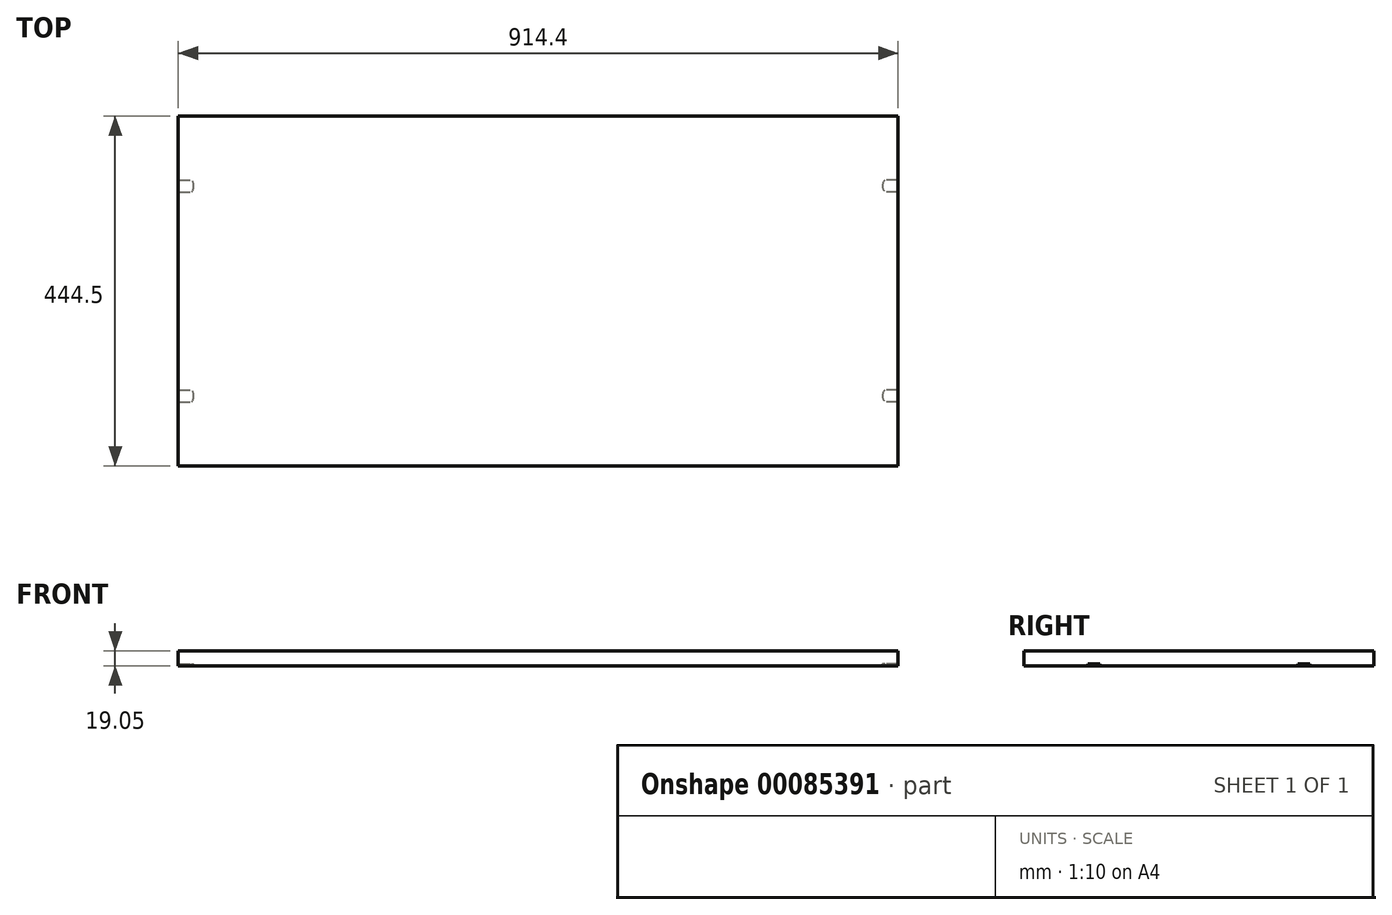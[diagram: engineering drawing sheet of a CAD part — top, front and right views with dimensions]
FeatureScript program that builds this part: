
annotation { "Feature Type Name" : "Feature", "Feature Type Description" : "" }
export const myFeature = defineFeature(function(context is Context, id is Id, definition is map)
    precondition{}
    {
        {
            var Q0;
            Q0=qCreatedBy(makeId("Top.planeOp"),FACE);
            var sketch = newSketch(context, id + "F0", { "sketchPlane" : qUnion([Q0])});
            skLineSegment(sketch, "E0.bottom", {"start": v(457.2, 222.25) * mm, "end": v(-457.2, 222.25) * mm});
            skLineSegment(sketch, "E0.top", {"start": v(457.2, -222.25) * mm, "end": v(-457.2, -222.25) * mm});
            skLineSegment(sketch, "E0.left", {"start": v(457.2, 222.25) * mm, "end": v(457.2, -222.25) * mm});
            skLineSegment(sketch, "E0.right", {"start": v(-457.2, 222.25) * mm, "end": v(-457.2, -222.25) * mm});
            skPoint(sketch, "E0.middle", {"position": v(0, 0) * mm});
            skLineSegment(sketch, "E1.bottom", {"start": v(-457.2, 126.87) * mm, "end": v(-440.94, 126.87) * mm});
            skLineSegment(sketch, "E1.top", {"start": v(-457.2, 139.83) * mm, "end": v(-440.94, 139.83) * mm});
            skLineSegment(sketch, "E1.left", {"start": v(-457.2, 126.87) * mm, "end": v(-457.2, 139.83) * mm});
            skLineSegment(sketch, "E1.right", {"start": v(-440.94, 126.87) * mm, "end": v(-440.94, 139.83) * mm});
            skArc(sketch, "E2", {"start": v(-440.94, 126.87) * mm, "mid": v(-438.66, 133.35) * mm, "end": v(-440.94, 139.83) * mm});
            skLineSegment(sketch, "E3.0", {"start": v(-457.2, 141.1) * mm, "end": v(-440.36, 141.1) * mm});
            skArc(sketch, "E4.0", {"start": v(-440.36, 125.6) * mm, "mid": v(-437.39, 133.35) * mm, "end": v(-440.36, 141.1) * mm});
            skLineSegment(sketch, "E5.0", {"start": v(-457.2, 125.6) * mm, "end": v(-440.36, 125.6) * mm});
            skLineSegment(sketch, "E6.bottom", {"start": v(-457.2, -139.83) * mm, "end": v(-440.94, -139.83) * mm});
            skLineSegment(sketch, "E6.top", {"start": v(-457.2, -126.87) * mm, "end": v(-440.94, -126.87) * mm});
            skLineSegment(sketch, "E6.left", {"start": v(-457.2, -139.83) * mm, "end": v(-457.2, -126.87) * mm});
            skLineSegment(sketch, "E6.right", {"start": v(-440.94, -139.83) * mm, "end": v(-440.94, -126.87) * mm});
            skArc(sketch, "E7", {"start": v(-440.94, -139.83) * mm, "mid": v(-438.66, -133.35) * mm, "end": v(-440.94, -126.87) * mm});
            skArc(sketch, "E8.0", {"start": v(-440.36, -141.1) * mm, "mid": v(-437.39, -133.35) * mm, "end": v(-440.36, -125.6) * mm});
            skLineSegment(sketch, "E9.0", {"start": v(-457.2, -141.1) * mm, "end": v(-440.36, -141.1) * mm});
            skLineSegment(sketch, "E10.0", {"start": v(-457.2, -125.6) * mm, "end": v(-440.36, -125.6) * mm});
            skArc(sketch, "E11.MirrorCS", {"start": v(-440.36, -125.6) * mm, "mid": v(-437.39, -133.35) * mm, "end": v(-440.36, -141.1) * mm});
            skArc(sketch, "E12.MirrorCS", {"start": v(-440.94, -126.87) * mm, "mid": v(-438.66, -133.35) * mm, "end": v(-440.94, -139.83) * mm});
            skLineSegment(sketch, "E13.MirrorCS", {"start": v(457.2, 141.1) * mm, "end": v(440.36, 141.1) * mm});
            skArc(sketch, "E14.MirrorCS", {"start": v(440.36, 125.6) * mm, "mid": v(437.39, 133.35) * mm, "end": v(440.36, 141.1) * mm});
            skLineSegment(sketch, "E15.MirrorCS", {"start": v(457.2, 125.6) * mm, "end": v(440.36, 125.6) * mm});
            skLineSegment(sketch, "E16.MirrorCS", {"start": v(457.2, -125.6) * mm, "end": v(440.36, -125.6) * mm});
            skArc(sketch, "E17.MirrorCS", {"start": v(440.36, -125.6) * mm, "mid": v(437.39, -133.35) * mm, "end": v(440.36, -141.1) * mm});
            skLineSegment(sketch, "E18.MirrorCS", {"start": v(457.2, -141.1) * mm, "end": v(440.36, -141.1) * mm});
            skSolve(sketch);
        }
        {
            var Q0;
            Q0 = qSketchRegion(id + "F0", true);
            var Q1;
            Q1=makeQuery(id+"F0.imprint","IMPRINT",FACE,{"disambiguationData":[TD([[makeQuery(id+"F0.imprint","IMPRINT",EDGE,{"derivedFrom":sQuery(id+"F0.wireOp",EDGE,"E1.right")}),-1.0]])]});
            var Q2;
            Q2=makeQuery(id+"F0.imprint","IMPRINT",FACE,{"disambiguationData":[TD([[makeQuery(id+"F0.imprint","IMPRINT",EDGE,{"derivedFrom":sQuery(id+"F0.wireOp",EDGE,"E6.right")}),-1.0]])]});
            extrude(context, id + "F1", {"entities" : qUnion([Q0, Q1, Q2]), "oppositeDirection" : true, "depth" : 16.5 * mm});
        }
        {
            var Q0;
            {var subQ4=sQuery(id+"F0.wireOp",EDGE,"E0.bottom");Q0=makeQuery(id+"F0.imprint","IMPRINT",FACE,{"disambiguationData":[TD([[makeQuery(id+"F0.imprint","IMPRINT",EDGE,{"derivedFrom":subQ4}),1.0]])]});}
            extrude(context, id + "F2", {"entities" : qUnion([Q0]), "operationType" : NewBodyOperationType.ADD, "oppositeDirection" : true, "depth" : 19.05 * mm});
        }
    });
